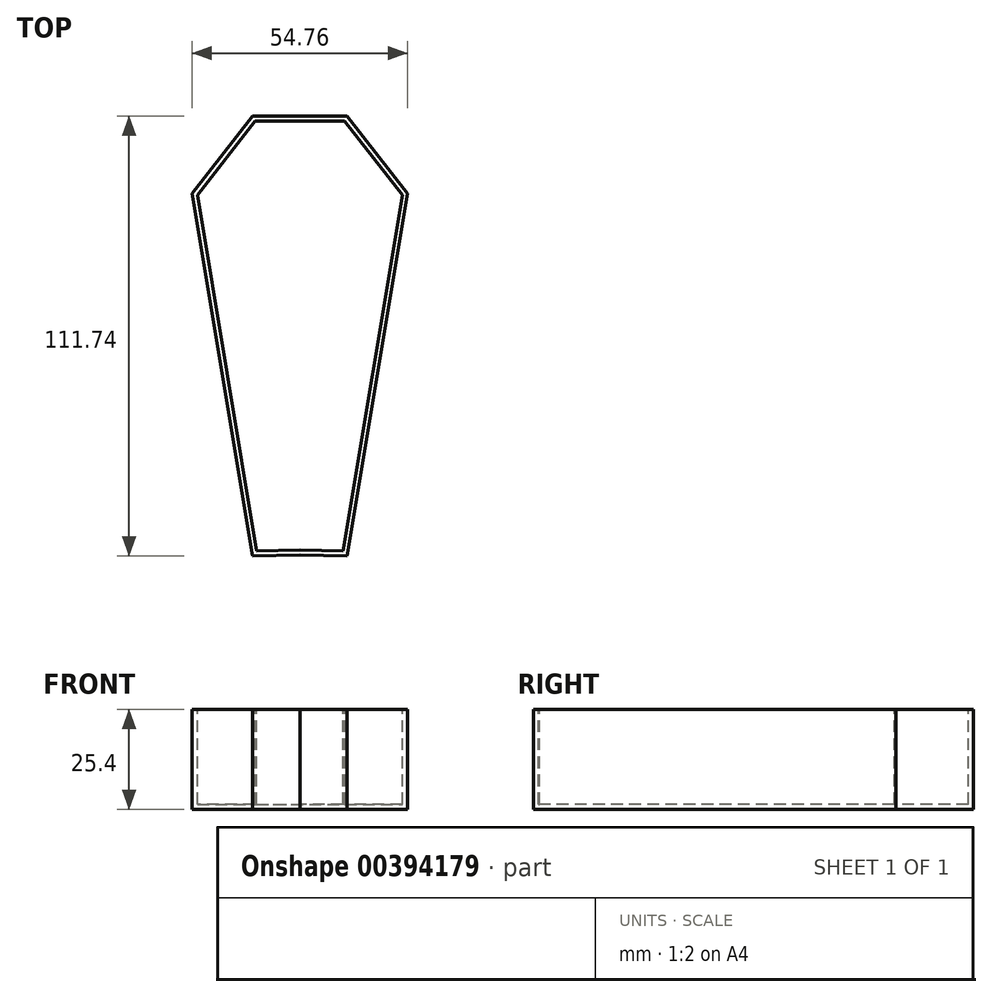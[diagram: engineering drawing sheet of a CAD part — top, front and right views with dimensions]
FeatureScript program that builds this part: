
annotation { "Feature Type Name" : "Feature", "Feature Type Description" : "" }
export const myFeature = defineFeature(function(context is Context, id is Id, definition is map)
    precondition{}
    {
        {
            var Q0;
            Q0=qCreatedBy(makeId("Top.planeOp"),FACE);
            var sketch = newSketch(context, id + "F0", { "sketchPlane" : qUnion([Q0])});
            skLineSegment(sketch, "E0", {"start": v(0, 55.97) * mm, "end": v(-12.01, 55.97) * mm});
            skLineSegment(sketch, "E1", {"start": v(-12.01, 55.97) * mm, "end": v(-27.38, 36.26) * mm});
            skLineSegment(sketch, "E2", {"start": v(-27.38, 36.26) * mm, "end": v(-12.01, -55.77) * mm});
            skLineSegment(sketch, "E3", {"start": v(-12.01, -55.77) * mm, "end": v(0, -55.57) * mm});
            skLineSegment(sketch, "E4.MirrorCS", {"start": v(27.38, 36.26) * mm, "end": v(12.01, -55.77) * mm});
            skLineSegment(sketch, "E5.MirrorCS", {"start": v(12.01, 55.97) * mm, "end": v(27.38, 36.26) * mm});
            skLineSegment(sketch, "E6.MirrorCS", {"start": v(0, 55.97) * mm, "end": v(12.01, 55.97) * mm});
            skLineSegment(sketch, "E7.MirrorCS", {"start": v(12.01, -55.77) * mm, "end": v(0, -55.57) * mm});
            skSolve(sketch);
        }
        {
            var Q0;
            Q0=makeQuery(id+"F0.imprint","IMPRINT",FACE,{"disambiguationData":[TD([[makeQuery(id+"F0.imprint","IMPRINT",EDGE,{"derivedFrom":sQuery(id+"F0.wireOp",EDGE,"E0")}),1.0]])]});
            extrude(context, id + "F1", {"entities" : qUnion([Q0]), "oppositeDirection" : true, "depth" : 25.4 * mm});
        }
        {
            var Q0;
            Q0=makeQuery(id+"F1.opExtrude","CAP_FACE",FACE,{"disambiguationData":[OSD([sQuery(id+"F0.wireOp",EDGE,"E0"),sQuery(id+"F0.wireOp",EDGE,"E1"),sQuery(id+"F0.wireOp",EDGE,"E2"),sQuery(id+"F0.wireOp",EDGE,"E3"),sQuery(id+"F0.wireOp",EDGE,"E4.MirrorCS"),sQuery(id+"F0.wireOp",EDGE,"E5.MirrorCS"),sQuery(id+"F0.wireOp",EDGE,"E6.MirrorCS"),sQuery(id+"F0.wireOp",EDGE,"E7.MirrorCS")])],"isStart":true});
            shell(context, id + "F2", {"entities" : qUnion([Q0]), "thickness" : 1.27 * mm});
        }
    });
